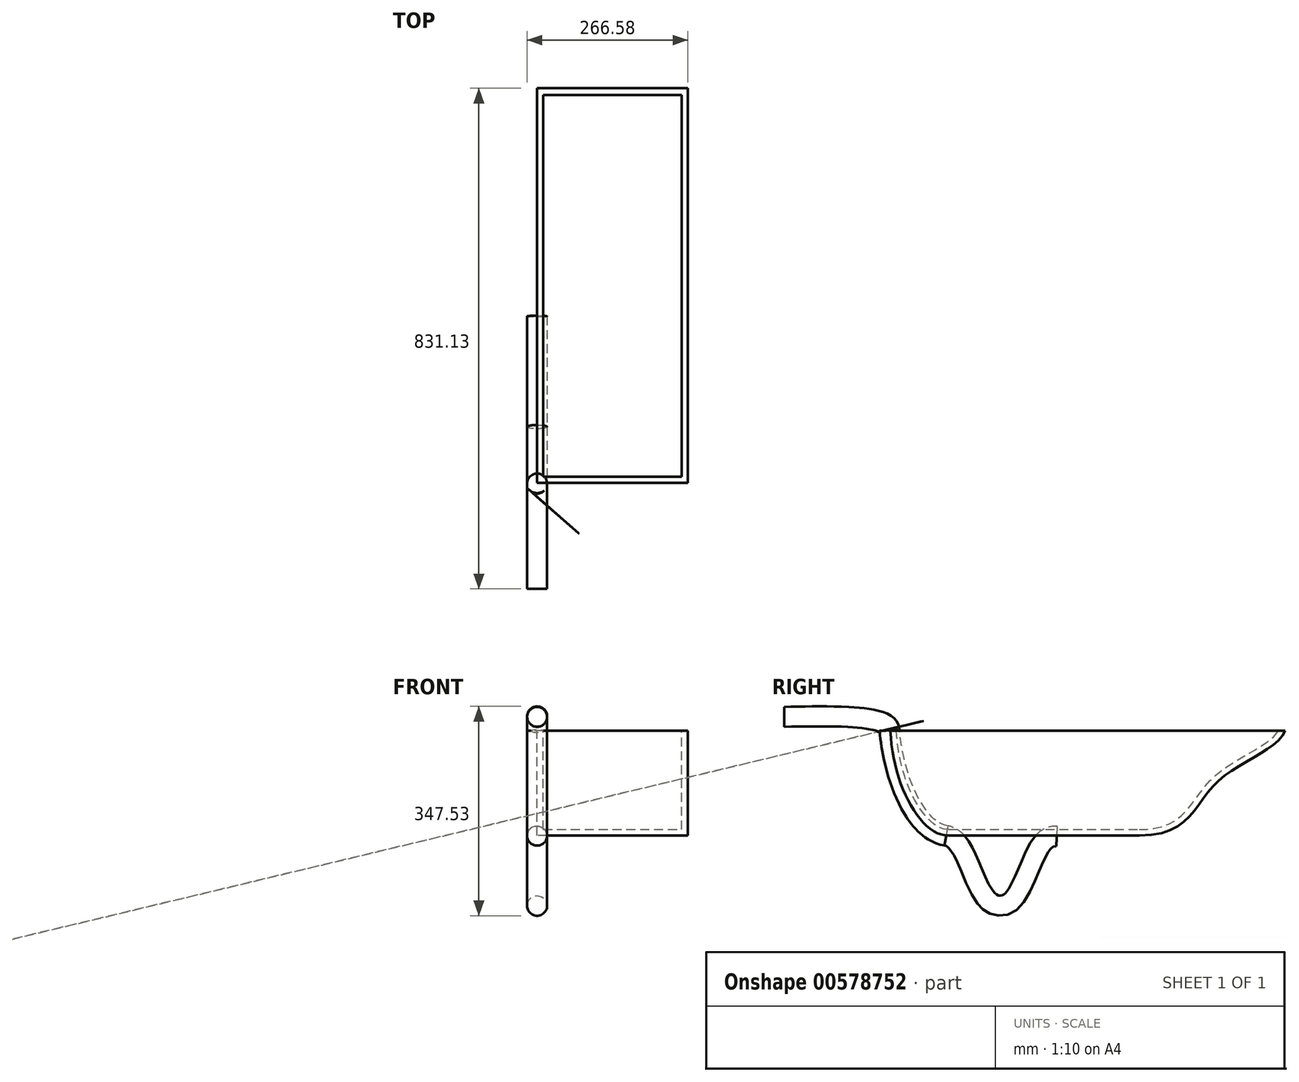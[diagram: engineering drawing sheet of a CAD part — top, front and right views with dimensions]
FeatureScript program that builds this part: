
annotation { "Feature Type Name" : "Feature", "Feature Type Description" : "" }
export const myFeature = defineFeature(function(context is Context, id is Id, definition is map)
    precondition{}
    {
        {
            var Q0;
            Q0=qCreatedBy(makeId("Right.planeOp"),FACE);
            var sketch = newSketch(context, id + "F0", { "sketchPlane" : qUnion([Q0])});
            skLineSegment(sketch, "E0", {"start": v(-222.78, -59.7) * mm, "end": v(94.02, -59.7) * mm});
            skFitSpline(sketch, "E1", {"points": [v(94.02, -59.7) * mm, v(223.9, 29.64) * mm, v(335.92, 114.16) * mm], "startDerivative": vector(493.7, 0) * mm, "endDerivative": vector(76.04, 196.8) * mm});
            skFitSpline(sketch, "E2", {"points": [v(-222.78, -59.7) * mm, v(-318.99, 114.16) * mm], "startDerivative": vector(-142.39, 0) * mm, "endDerivative": vector(-10.3, 261.82) * mm});
            skLineSegment(sketch, "E3", {"start": v(-318.99, 114.16) * mm, "end": v(335.92, 114.16) * mm});
            skSolve(sketch);
        }
        {
            var Q0;
            Q0=qSketchRegion(id+"F0",true);
            extrude(context, id + "F1", {"entities" : qUnion([Q0]), "depth" : 250 * mm, "offsetDistance" : 25 * mm});
        }
        {
            var Q0;
            Q0=makeQuery(id+"F1.opExtrude","SWEPT_FACE",FACE,{"disambiguationData":[OSD([sQuery(id+"F0.wireOp",EDGE,"E3")])]});
            shell(context, id + "F2", {"entities" : qUnion([Q0]), "thickness" : 10 * mm});
        }
        {
            var Q0;
            Q0=qCreatedBy(makeId("Right.planeOp"),FACE);
            var sketch = newSketch(context, id + "F3", { "sketchPlane" : qUnion([Q0])});
            skFitSpline(sketch, "E4", {"points": [v(-320.32, 115.12) * mm, v(-226.27, -60) * mm], "startDerivative": vector(19.69, -239.1) * mm, "endDerivative": vector(158.31, -26.65) * mm});
            skFitSpline(sketch, "E5", {"points": [v(-226.27, -60) * mm, v(-199.67, -83.36) * mm, v(-162.7, -160.55) * mm, v(-136.76, -176.11) * mm, v(-112.1, -161.84) * mm, v(-74.49, -84) * mm, v(-42.7, -60.66) * mm], "startDerivative": vector(218.22, -36.73) * mm, "endDerivative": vector(296.58, -12.9) * mm});
            skFitSpline(sketch, "E6", {"points": [v(-320.32, 115.12) * mm, v(-339.02, 130.51) * mm, v(-495.2, 137.4) * mm], "startDerivative": vector(-6.2, 75.3) * mm, "endDerivative": vector(-272, -6.5) * mm});
            skLineSegment(sketch, "E7", {"start": v(-495.2, 137.4) * mm, "end": v(-495.2, 163.97) * mm});
            skSolve(sketch);
        }
        {
            var Q0;
            Q0=sQuery(id+"F3.wireOp",EDGE,"E7");
            cPlane(context, id + "F4", {"entities" : qUnion([Q0]), "cplaneType" : CPlaneType.LINE_ANGLE, "offset" : 25 * mm, "angle" : 90 * degree, "width" : 150 * mm, "height" : 150 * mm});
        }
        {
            var Q0;
            Q0=qCreatedBy(id+"F4.planeOp",FACE);
            var sketch = newSketch(context, id + "F5", { "sketchPlane" : qUnion([Q0])});
            skCircle(sketch, "E8", {"center": v(0, 137.42) * mm, "radius": 16.58 * mm});
            skSolve(sketch);
        }
        {
            var Q0;
            Q0=makeQuery(id+"F5.imprint","IMPRINT",FACE,{"disambiguationData":[TD([[makeQuery(id+"F5.imprint","IMPRINT",EDGE,{"derivedFrom":sQuery(id+"F5.wireOp",EDGE,"E8")}),1.0]])]});
            var Q1;
            Q1=sQuery(id+"F3.wireOp",EDGE,"E6");
            var Q2;
            Q2=sQuery(id+"F3.wireOp",EDGE,"E4");
            var Q3;
            Q3=sQuery(id+"F3.wireOp",EDGE,"E5");
            sweep(context, id + "F6", {"profiles" : qUnion([Q0]), "path" : qUnion([Q1, Q2, Q3])});
        }
    });
